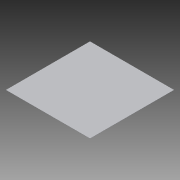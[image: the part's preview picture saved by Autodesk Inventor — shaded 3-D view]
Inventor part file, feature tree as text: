
AUTODESK INVENTOR PART (.ipt)
format: ipt  version: 2013 (Build 170138000, 138)  size: 74,240 bytes
history: native  units: in
note: dims shown in document units (in); Inventor stores cm internally (conversion verified against a paired STEP export)
features: sheet_metal_op x1, sketch x1, other x1
ambient origin geometry x8: Origin, YZ Plane, XZ Plane, XY Plane, X Axis, Y Axis, Z Axis, Center Point
bodies: Solid1 (feature_tree)
feature tree (3):
  sheet_metal_op  "Face1"
  sketch  "Sketch1"  dims[d0=47.8125in d1=47.8125in d2=0.0938in]
  other  "Plate1"
